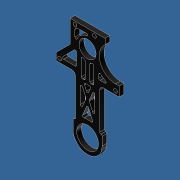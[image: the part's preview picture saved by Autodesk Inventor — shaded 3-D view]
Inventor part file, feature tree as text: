
AUTODESK INVENTOR PART (.ipt)
format: ipt  version: unknown  size: 654,848 bytes
history: native  units: in
note: dims shown in document units (in); Inventor stores cm internally (conversion verified against a paired STEP export)
features: sketch x25, extrude x23, fillet x14, hole x2, reference x1, projected_geometry x1
ambient origin geometry x8: Origin, YZ Plane, XZ Plane, XY Plane, X Axis, Y Axis, Z Axis, Center Point
bodies: Solid1 (feature_tree)
feature tree (66):
  extrude  "Extrusion1"  Depth=3.5in
  extrude  "Extrusion2"  Depth=1.25in
  extrude  "Extrusion3"  Depth=1.125in
  extrude  "Extrusion4"  Depth=3.25in
  extrude  "Extrusion5"  Depth=1.124in
  hole  "Hole1"  [1 undecoded]
  extrude  "Extrusion8"  Depth=0.125in
  extrude  "Extrusion9"  Depth=1.0in TaperAngle=0.0deg
  extrude  "Extrusion10"  Depth=1.625in
  extrude  "Extrusion11"  Depth=1.0in TaperAngle=0.0deg
  extrude  "Extrusion12"  Depth=0.1812in
  hole  "Hole2"  [1 undecoded]
  extrude  "Extrusion15"  Depth=0.125in
  extrude  "Extrusion17"  Depth=0.125in
  extrude  "Extrusion18"  Depth=2.25in
  extrude  "Extrusion19"  Depth=1.6732in
  fillet  "Fillet15"  Radius=1.0in
  extrude  "Extrusion20"  Depth=1.0in TaperAngle=0.0deg
  extrude  "Extrusion21"  Depth=0.3625in
  fillet  "Fillet18"  Radius=0.726in
  extrude  "Extrusion22"  Depth=0.1625in
  fillet  "Fillet19"  Radius=0.1625in
  fillet  "Fillet20"  Radius=0.25in
  fillet  "Fillet22"  Radius=1.0in
  extrude  "Extrusion23"  Depth=0.649in
  fillet  "Fillet25"  [1 undecoded]
  extrude  "Extrusion24"  Depth=0.25in
  fillet  "Fillet26"  Radius=0.0625in
  extrude  "Extrusion25"  Depth=0.125in
  extrude  "Extrusion27"  Depth=0.125in
  extrude  "Extrusion28"  Depth=0.125in TaperAngle=0.0deg
  extrude  "Extrusion29"  Depth=0.649in
  fillet  "Fillet27"  Radius=0.125in
  fillet  "Fillet28"  Radius=0.125in
  fillet  "Fillet29"  Radius=0.25in
  fillet  "Fillet30"  Radius=0.25in
  fillet  "Fillet31"  Radius=0.0625in
  fillet  "Fillet32"  Radius=0.075in
  fillet  "Fillet33"  Radius=0.075in
  sketch  "Sketch1"  dims[d0=5.5in d1=3.5in]
  sketch  "Sketch2"  dims[d2=0.25in d3=0.0in d4=1.25in]
  sketch  "Sketch3"  dims[d5=1.125in d6=1.125in]
  sketch  "Sketch4"  dims[d7=3.25in d8=3.25in]
  sketch  "Sketch5"  dims[d9=0.25in d10=0.0in d11=1.124in]
  sketch  "Sketch8"  dims[d12=0.625in d13=0.625in]
  sketch  "Sketch9"  dims[d14=1.0in d15=0.0in d16=0.125in]
  sketch  "Sketch10"  dims[d17=0.125in d18=1.0in d19=0.0in]
  reference  "Reference1"
  sketch  "Sketch11"  dims[d20=1.325in d21=1.625in]
  sketch  "Sketch12"  dims[d22=0.874in d23=1.0in d24=0.0in]
  sketch  "Sketch13"  dims[d33=0.1875in d34=0.1812in]
  sketch  "Sketch14"  dims[d35=0.1875in d36=0.1812in]
  sketch  "Sketch17"  dims[d37=0.196in d38=0.75in d39=0.385in d40=0.25in d41=0.5635in d42=1.0in d43=0.8108in d44=0.125in]
  sketch  "Sketch22"  dims[d45=0.125in d46=0.125in]
  sketch  "Sketch23"  dims[d48=2.25in d49=2.25in]
  projected_geometry  "Projected Loop2"
  sketch  "Sketch24"  dims[d50=0.25in d51=0.0in d61=1.6732in d62=1.0in d63=0.0in]
  sketch  "Sketch25"  dims[d64=0.726in d65=1.0in d66=0.0in]
  sketch  "Sketch26"  dims[d67=1.0in d68=0.0in d72=0.3625in d73=0.726in]
  sketch  "Sketch27"  dims[d74=1.0in d75=0.0in d77=0.1625in d78=0.1625in d79=0.25in d80=1.0in]
  sketch  "Sketch28"  dims[d81=0.351in d82=0.649in]
  sketch  "Sketch29"  dims[d83=0.196in d84=0.75in d85=0.385in d86=0.25in d87=0.5635in d88=1.0in d89=0.8108in d105=45.0deg]
  sketch  "Sketch30"  dims[d106=0.25in d107=0.0in d121=0.25in d122=0.0625in]
  sketch  "Sketch32"  dims[d123=0.0625in d124=0.125in]
  sketch  "Sketch33"  dims[d125=0.0625in d128=0.125in]
  sketch  "Sketch34"  dims[d129=0.25in d130=0.0in d131=0.0in d132=0.125in d133=0.125in d138=0.649in d139=0.125in d140=0.125in d141=0.25in d142=0.0in d143=0.25in d144=0.0in d145=0.0625in d146=0.075in d147=0.075in d148=0.075in d149=0.075in d150=0.25in d151=0.0in d152=0.125in d153=0.125in d154=0.25in d155=0.0in d158=0.0625in d159=0.25in d160=0.0in d161=0.0625in d162=0.0625in d164=0.75in d167=0.25in d168=0.25in d169=0.25in d170=0.0in d171=0.0625in d172=0.5in d173=0.5in d174=0.25in d175=0.0in d176=0.0625in d177=1.4in d178=1.4in d179=0.625in d180=0.625in d181=0.1in d182=0.1in d183=0.1in d184=0.1in d185=0.1375in d186=0.1375in d187=0.625in d188=0.25in d189=0.0in d193=0.25in d194=0.25in d195=0.25in d196=0.0in d197=0.05in d198=0.25in d199=0.0in d200=0.125in d201=0.25in d202=0.0in d203=0.0625in d204=0.0625in d205=0.0625in d206=0.0625in d207=0.1875in d208=0.0625in d209=0.0625in d210=0.2in]
note: 3 required parameter values undecoded (feature->parameter linkage not recoverable at this tier; creation-order binding heuristic only, values carry confidence <= 0.55)
